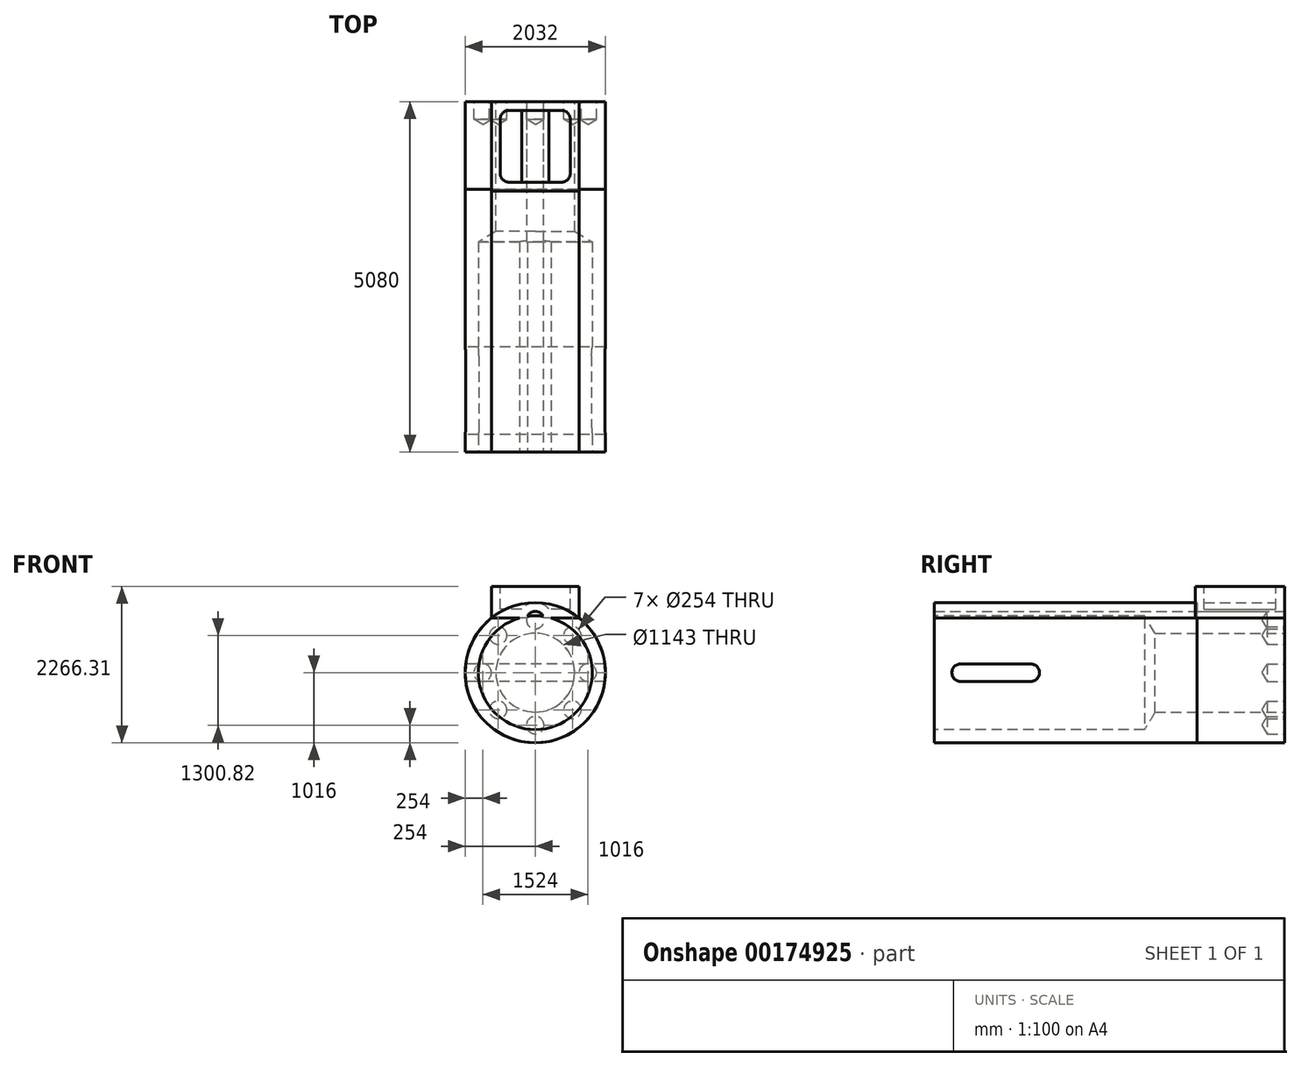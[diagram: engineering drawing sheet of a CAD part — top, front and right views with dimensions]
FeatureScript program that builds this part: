
annotation { "Feature Type Name" : "Feature", "Feature Type Description" : "" }
export const myFeature = defineFeature(function(context is Context, id is Id, definition is map)
    precondition{}
    {
        {
            var Q0;
            Q0=qCreatedBy(makeId("Front.planeOp"),FACE);
            var sketch = newSketch(context, id + "F0", { "sketchPlane" : qUnion([Q0])});
            skPoint(sketch, "E0.first.point", {"position": v(0, 0) * mm});
            skLineSegment(sketch, "E1", {"start": v(635, 793.11) * mm, "end": v(635, 1250.31) * mm});
            skLineSegment(sketch, "E2.MirrorCS", {"start": v(-635, 793.11) * mm, "end": v(-635, 1250.31) * mm});
            skLineSegment(sketch, "E3", {"start": v(635, 1250.31) * mm, "end": v(-635, 1250.31) * mm});
            skLineSegment(sketch, "E4", {"start": v(635, 793.11) * mm, "end": v(-635, 793.11) * mm});
            skArc(sketch, "E5", {"start": v(635, 793.11) * mm, "mid": v(0, -1016) * mm, "end": v(-635, 793.11) * mm});
            skCircle(sketch, "E6", {"center": v(0, 762) * mm, "radius": 127 * mm});
            skCircle(sketch, "E7.1.0", {"center": v(-538.82, 538.82) * mm, "radius": 127 * mm});
            skCircle(sketch, "E7.2.0", {"center": v(-762, 0) * mm, "radius": 127 * mm});
            skCircle(sketch, "E7.3.0", {"center": v(-538.82, -538.82) * mm, "radius": 127 * mm});
            skCircle(sketch, "E7.4.0", {"center": v(0, -762) * mm, "radius": 127 * mm});
            skCircle(sketch, "E7.5.0", {"center": v(538.82, -538.82) * mm, "radius": 127 * mm});
            skCircle(sketch, "E7.6.0", {"center": v(762, 0) * mm, "radius": 127 * mm});
            skCircle(sketch, "E7.7.0", {"center": v(538.82, 538.82) * mm, "radius": 127 * mm});
            skSolve(sketch);
        }
        {
            var Q0;
            {var subQ0=sQuery(id+"F0.wireOp",EDGE,"E4");Q0=makeQuery(id+"F0.imprint","IMPRINT",FACE,{"disambiguationData":[TD([[makeQuery(id+"F0.imprint","IMPRINT",EDGE,{"derivedFrom":subQ0}),1.0]])]});}
            var Q1;
            Q1=makeQuery(id+"F0.imprint","IMPRINT",FACE,{"disambiguationData":[TD([[makeQuery(id+"F0.imprint","IMPRINT",EDGE,{"derivedFrom":sQuery(id+"F0.wireOp",EDGE,"E7.7.0")}),1.0]])]});
            var Q2;
            Q2=makeQuery(id+"F0.imprint","IMPRINT",FACE,{"disambiguationData":[TD([[makeQuery(id+"F0.imprint","IMPRINT",EDGE,{"derivedFrom":sQuery(id+"F0.wireOp",EDGE,"E7.6.0")}),1.0]])]});
            var Q3;
            Q3=makeQuery(id+"F0.imprint","IMPRINT",FACE,{"disambiguationData":[TD([[makeQuery(id+"F0.imprint","IMPRINT",EDGE,{"derivedFrom":sQuery(id+"F0.wireOp",EDGE,"E7.5.0")}),1.0]])]});
            var Q4;
            Q4=makeQuery(id+"F0.imprint","IMPRINT",FACE,{"disambiguationData":[TD([[makeQuery(id+"F0.imprint","IMPRINT",EDGE,{"derivedFrom":sQuery(id+"F0.wireOp",EDGE,"E7.4.0")}),1.0]])]});
            var Q5;
            Q5=makeQuery(id+"F0.imprint","IMPRINT",FACE,{"disambiguationData":[TD([[makeQuery(id+"F0.imprint","IMPRINT",EDGE,{"derivedFrom":sQuery(id+"F0.wireOp",EDGE,"E7.3.0")}),1.0]])]});
            var Q6;
            Q6=makeQuery(id+"F0.imprint","IMPRINT",FACE,{"disambiguationData":[TD([[makeQuery(id+"F0.imprint","IMPRINT",EDGE,{"derivedFrom":sQuery(id+"F0.wireOp",EDGE,"E7.2.0")}),1.0]])]});
            var Q7;
            Q7=makeQuery(id+"F0.imprint","IMPRINT",FACE,{"disambiguationData":[TD([[makeQuery(id+"F0.imprint","IMPRINT",EDGE,{"derivedFrom":sQuery(id+"F0.wireOp",EDGE,"E7.1.0")}),1.0]])]});
            var Q8;
            {var subQ0=sQuery(id+"F0.wireOp",EDGE,"E6");var subQ1=sQuery(id+"F0.wireOp",EDGE,"E4");var subQ2=makeQuery(id+"F0.imprint","INTERSECT",VERTEX,{"disambiguationData":[OD(0.0)],"derivedFrom":[subQ1,subQ0]});Q8=makeQuery(id+"F0.imprint","IMPRINT",FACE,{"disambiguationData":[TD([[makeQuery(id+"F0.imprint","IMPRINT",EDGE,{"disambiguationData":[TD([[subQ2,-1.0]])],"derivedFrom":subQ1}),-1.0]])]});}
            var Q9;
            {var subQ0=sQuery(id+"F0.wireOp",EDGE,"E6");var subQ1=sQuery(id+"F0.wireOp",EDGE,"E4");var subQ2=makeQuery(id+"F0.imprint","INTERSECT",VERTEX,{"disambiguationData":[OD(0.0)],"derivedFrom":[subQ1,subQ0]});Q9=makeQuery(id+"F0.imprint","IMPRINT",FACE,{"disambiguationData":[TD([[makeQuery(id+"F0.imprint","IMPRINT",EDGE,{"disambiguationData":[TD([[subQ2,-1.0]])],"derivedFrom":subQ1}),1.0]])]});}
            extrude(context, id + "F1", {"entities" : qUnion([Q0, Q1, Q2, Q3, Q4, Q5, Q6, Q7, Q8, Q9]), "depth" : 5080 * mm});
        }
        {
            var Q0;
            {var subQ1=sQuery(id+"F0.wireOp",EDGE,"E1");Q0=makeQuery(id+"F0.imprint","IMPRINT",FACE,{"disambiguationData":[TD([[makeQuery(id+"F0.imprint","IMPRINT",EDGE,{"derivedFrom":subQ1}),1.0]])]});}
            var Q1;
            {var subQ0=sQuery(id+"F0.wireOp",EDGE,"E4");Q1=makeQuery(id+"F0.imprint","IMPRINT",FACE,{"disambiguationData":[TD([[makeQuery(id+"F0.imprint","IMPRINT",EDGE,{"derivedFrom":subQ0}),-1.0]])]});}
            extrude(context, id + "F2", {"entities" : qUnion([Q0, Q1]), "depth" : 1295.4 * mm});
        }
        {
            var Q0;
            Q0=makeQuery(id+"F2.opExtrude","SWEPT_FACE",FACE,{"disambiguationData":[OSD([sQuery(id+"F0.wireOp",EDGE,"E3")])]});
            shell(context, id + "F3", {"entities" : qUnion([Q0]), "thickness" : 127 * mm});
        }
        {
            var Q0;
            Q0=makeQuery(id+"F1.opExtrude","CAP_FACE",FACE,{"disambiguationData":[OSD([sQuery(id+"F0.wireOp",EDGE,"E4"),sQuery(id+"F0.wireOp",EDGE,"E5")])],"isStart":false});
            var sketch = newSketch(context, id + "F4", { "sketchPlane" : qUnion([Q0])});
            skCircle(sketch, "E8", {"center": v(0, 0) * mm, "radius": 1016 * mm});
            skSolve(sketch);
        }
        {
            var Q0;
            Q0=makeQuery(id+"F4.imprint","IMPRINT",FACE,{"disambiguationData":[TD([[makeQuery(id+"F4.imprint","IMPRINT",EDGE,{"disambiguationData":[OD(1.0)],"derivedFrom":sQuery(id+"F4.wireOp",EDGE,"E8")}),1.0]])]});
            extrude(context, id + "F5", {"entities" : qUnion([Q0]), "oppositeDirection" : true, "depth" : 3810 * mm});
        }
        {
            var Q0;
            {var subQ0=sQuery(id+"F0.wireOp",EDGE,"E2.MirrorCS");Q0=makeQuery(id+"F3.opShell","OFFSET_EDGE",EDGE,{"disambiguationData":[OSD([subQ0]),TDD([makeQuery(id+"F2.opExtrude","CAP_EDGE",EDGE,{"disambiguationData":[OSD([subQ0])],"isStart":true})])]});}
            var Q1;
            {var subQ0=sQuery(id+"F0.wireOp",EDGE,"E1");Q1=makeQuery(id+"F3.opShell","OFFSET_EDGE",EDGE,{"disambiguationData":[OSD([subQ0]),TDD([makeQuery(id+"F2.opExtrude","CAP_EDGE",EDGE,{"disambiguationData":[OSD([subQ0])],"isStart":true})])]});}
            var Q2;
            {var subQ0=sQuery(id+"F0.wireOp",EDGE,"E1");Q2=makeQuery(id+"F3.opShell","OFFSET_EDGE",EDGE,{"disambiguationData":[OSD([subQ0]),TDD([makeQuery(id+"F2.opExtrude","CAP_EDGE",EDGE,{"disambiguationData":[OSD([subQ0])],"isStart":false})])]});}
            var Q3;
            {var subQ0=sQuery(id+"F0.wireOp",EDGE,"E2.MirrorCS");Q3=makeQuery(id+"F3.opShell","OFFSET_EDGE",EDGE,{"disambiguationData":[OSD([subQ0]),TDD([makeQuery(id+"F2.opExtrude","CAP_EDGE",EDGE,{"disambiguationData":[OSD([subQ0])],"isStart":false})])]});}
            fillet(context, id + "F6", {"entities" : qUnion([Q0, Q1, Q2, Q3]), "radius" : 127 * mm, "tangentPropagation" : true, "allowEdgeOverflow" : false});
        }
        {
            var Q0;
            Q0=sQuery(id+"F0.wireOp",VERTEX,"E0.first.point");
            var Q1;
            Q1=makeQuery(id+"F1.opExtrude","SWEPT_BODY",BODY,{"disambiguationData":[OSD([sQuery(id+"F0.wireOp",EDGE,"E4"),sQuery(id+"F0.wireOp",EDGE,"E5")])]});
            hole(context, id + "F7", {"style" : HoleStyle.SIMPLE, "endStyle" : HoleEndStyle.THROUGH, "oppositeDirection" : true, "holeDiameter" : 1143 * mm, "locations" : qUnion([Q0]), "scope" : qUnion([Q1]), "isTappedThrough" : true});
        }
        {
            var Q0;
            Q0=sQuery(id+"F4.wireOp",VERTEX,"E8.center");
            var Q1;
            Q1=makeQuery(id+"F1.opExtrude","SWEPT_BODY",BODY,{"disambiguationData":[OSD([sQuery(id+"F0.wireOp",EDGE,"E4"),sQuery(id+"F0.wireOp",EDGE,"E5")])]});
            hole(context, id + "F8", {"style" : HoleStyle.SIMPLE, "endStyle" : HoleEndStyle.BLIND, "holeDiameter" : 1651 * mm, "holeDepth" : 3048 * mm, "locations" : qUnion([Q0]), "scope" : qUnion([Q1])});
        }
        {
            var Q0;
            Q0=sQuery(id+"F0.wireOp",VERTEX,"E7.7.0.center");
            var Q1;
            Q1=sQuery(id+"F0.wireOp",VERTEX,"E6.center");
            var Q2;
            Q2=sQuery(id+"F0.wireOp",VERTEX,"E7.1.0.center");
            var Q3;
            Q3=sQuery(id+"F0.wireOp",VERTEX,"E7.2.0.center");
            var Q4;
            Q4=sQuery(id+"F0.wireOp",VERTEX,"E7.3.0.center");
            var Q5;
            Q5=sQuery(id+"F0.wireOp",VERTEX,"E7.4.0.center");
            var Q6;
            Q6=sQuery(id+"F0.wireOp",VERTEX,"E7.5.0.center");
            var Q7;
            Q7=sQuery(id+"F0.wireOp",VERTEX,"E7.6.0.center");
            var Q8;
            Q8=makeQuery(id+"F1.opExtrude","SWEPT_BODY",BODY,{"disambiguationData":[OSD([sQuery(id+"F0.wireOp",EDGE,"E4"),sQuery(id+"F0.wireOp",EDGE,"E5"),sQuery(id+"F0.wireOp",EDGE,"E6")])]});
            hole(context, id + "F9", {"style" : HoleStyle.SIMPLE, "endStyle" : HoleEndStyle.BLIND, "oppositeDirection" : true, "holeDiameter" : 254 * mm, "majorDiameter" : 6.35 * mm, "holeDepth" : 254 * mm, "startFromSketch" : true, "locations" : qUnion([Q0, Q1, Q2, Q3, Q4, Q5, Q6, Q7]), "scope" : qUnion([Q8]), "tappedDepth" : 12.7 * mm, "tapClearance" : 3});
        }
        {
            var Q0;
            Q0=qCreatedBy(makeId("Right.planeOp"),FACE);
            var sketch = newSketch(context, id + "F10", { "sketchPlane" : qUnion([Q0])});
            skLineSegment(sketch, "E9", {"start": v(-3683, 0) * mm, "end": v(-3683, 127) * mm});
            skLineSegment(sketch, "E10", {"start": v(-4699, 0) * mm, "end": v(-4699, 127) * mm});
            skLineSegment(sketch, "E11", {"start": v(-3683, 127) * mm, "end": v(-4699, 127) * mm});
            skLineSegment(sketch, "E12.MirrorCS", {"start": v(-3683, 0) * mm, "end": v(-3683, -127) * mm});
            skLineSegment(sketch, "E13.MirrorCS", {"start": v(-3683, -127) * mm, "end": v(-4699, -127) * mm});
            skLineSegment(sketch, "E14.MirrorCS", {"start": v(-4699, 0) * mm, "end": v(-4699, -127) * mm});
            skArc(sketch, "E15", {"start": v(-3683, 127) * mm, "mid": v(-3556, 0) * mm, "end": v(-3683, -127) * mm});
            skArc(sketch, "E16", {"start": v(-4699, 127) * mm, "mid": v(-4826, 0) * mm, "end": v(-4699, -127) * mm});
            skSolve(sketch);
        }
        {
            var Q0;
            Q0 = qSketchRegion(id + "F10", true);
            extrude(context, id + "F11", {"entities" : qUnion([Q0]), "operationType" : NewBodyOperationType.REMOVE, "endBound" : BoundingType.SYMMETRIC, "depth" : 2540 * mm});
        }
    });
